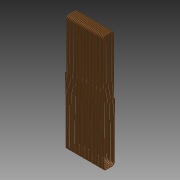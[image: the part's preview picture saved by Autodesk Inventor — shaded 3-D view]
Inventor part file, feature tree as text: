
AUTODESK INVENTOR PART (.ipt)
format: ipt  version: 2015 (Build 190159000, 159)  size: 2,329,600 bytes
history: native  units: in
note: dims shown in document units (in); Inventor stores cm internally (conversion verified against a paired STEP export)
features: sweep x1, other x1, imported_body x1
ambient origin geometry x8: Origin, YZ Plane, XZ Plane, XY Plane, X Axis, Y Axis, Z Axis, Center Point
bodies: Body1 (feature_tree)
feature tree (3):
  sweep  "Sweep4"
  other  "Stator_Coil.ipt1"
  imported_body  "Base1"
